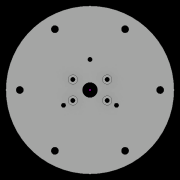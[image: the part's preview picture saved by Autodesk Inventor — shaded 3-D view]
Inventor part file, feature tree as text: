
AUTODESK INVENTOR PART (.ipt)
format: ipt  version: 2022.2 (Build 262287010, 287A)  size: 654,848 bytes
history: native  units: mm
features: extrude x31, sketch x22, other x19, pattern_circular x11, plane x8, fillet x2, move_body x2, revolve x2, draft x2, chamfer x2
ambient origin geometry x8: Origin, YZ Plane, XZ Plane, XY Plane, X Axis, Y Axis, Z Axis, Center Point
bodies: Solid5 (feature_tree)
feature tree (101):
  other  "CrossSection1"
  sketch  "Sketch7"  dims[d167=8.972256mm]
  other  "Roller1"
  other  "Roller2"
  sketch  "Sketch22"  dims[d173=10.814812mm]
  sketch  "Sketch2"  dims[d57=4.025mm d90=61.984365mm]
  sketch  "Sketch23"  dims[d201=75.0mm d232=0.0mm d233=3600.0mm]
  other  "RevRoller1"
  fillet  "Fillet1"  Radius=59.246882mm
  extrude  "Extrusion39"  Depth=61.984365mm
  pattern_circular  "Circular Pattern13"  Count=360  [1 undecoded]
  move_body  "Move Body7"
  revolve  "Revolution13"  [1 undecoded]
  fillet  "Fillet3"  Radius=0.025mm
  pattern_circular  "Circular Pattern14"  Count=24  [1 undecoded]
  move_body  "Move Body6"
  revolve  "Revolution14"  [1 undecoded]
  other  "OuterRim_Top2"
  other  "OuterRim_Bottom2"
  plane  "Work Plane8"
  sketch  "Sketch49"  dims[d352=0.025mm]
  sketch  "Sketch50"  dims[d354=0.025mm]
  sketch  "Sketch51"  dims[d355=16.1595mm]
  extrude  "Extrusion40"  Depth=0.025mm
  extrude  "Extrusion41"  Depth=1.308997mm
  extrude  "Extrusion42"  Depth=0.5mm
  extrude  "Extrusion43"  TaperAngle=360.0deg  [1 undecoded]
  sketch  "Sketch52"  dims[d356=16.159664mm]
  extrude  "Extrusion44"  TaperAngle=90.0deg  [1 undecoded]
  extrude  "Extrusion45"  Depth=2.0mm
  extrude  "Extrusion46"  Depth=2.0mm
  extrude  "Extrusion47"  Depth=2.0mm
  pattern_circular  "Circular Pattern32"  [2 undecoded]
  pattern_circular  "Circular Pattern33"  [2 undecoded]
  sketch  "Sketch57"  dims[d358=360.0deg]
  extrude  "Extrusion50"  Depth=2.0mm
  extrude  "Extrusion51"  TaperAngle=0.0deg  [1 undecoded]
  pattern_circular  "Circular Pattern34"  [2 undecoded]
  extrude  "Extrusion52"  Depth=2.0mm
  extrude  "Extrusion53"  Depth=2.0mm
  pattern_circular  "Circular Pattern35"  [2 undecoded]
  plane  "Work Plane9"
  extrude  "Extrusion54"  Depth=2.0mm
  plane  "Work Plane10"
  sketch  "Sketch60"  dims[d367=8.1mm d370=0.025mm]
  plane  "Work Plane11"
  sketch  "Sketch61"  dims[d371=1.0mm d372=1.308997mm]
  plane  "Work Plane12"
  sketch  "Sketch62"  dims[d373=90.0deg d374=0.5mm]
  extrude  "Extrusion57"  Depth=2.0mm
  extrude  "Extrusion58"  Depth=2.0mm
  plane  "Work Plane7"
  sketch  "Sketch47"  dims[d350=47.575427mm]
  extrude  "Rotor_Ring"  TaperAngle=90.0deg  [1 undecoded]
  draft  "FaceDraft2"
  sketch  "Sketch30"  dims[d343=16.1595mm d344=16.159664mm d345=0.025mm]
  plane  "Work Plane5"
  other  "Rotor Featurs"
  other  "RotorRim_Bottom"
  extrude  "Extrusion24"  TaperAngle=90.0deg  [1 undecoded]
  extrude  "Extrusion25"  TaperAngle=90.0deg  [1 undecoded]
  extrude  "Extrusion26"  Depth=2.0mm
  pattern_circular  "Circular Pattern23"  [2 undecoded]
  sketch  "Sketch41"  dims[d347=0.1mm]
  extrude  "Extrusion27"  TaperAngle=0.0deg  [1 undecoded]
  extrude  "Extrusion28"  Depth=2.0mm
  pattern_circular  "Circular Pattern24"  Count=2  [1 undecoded]
  extrude  "Extrusion29"  Depth=2.5mm
  extrude  "Extrusion30"  Depth=2.0mm
  extrude  "Extrusion31"  Depth=2.0mm
  pattern_circular  "Circular Pattern25"  Angle=30.0deg  [1 undecoded]
  sketch  "Sketch42"  dims[d348=0.1mm]
  extrude  "Extrusion32"  Depth=2.0mm
  extrude  "Extrusion33"  Depth=2.0mm TaperAngle=30.0deg
  extrude  "Extrusion34"  Depth=2.0mm
  extrude  "Extrusion35"  Depth=2.0mm
  pattern_circular  "Circular Pattern26"  [2 undecoded]
  pattern_circular  "Circular Pattern27"  Count=10  [1 undecoded]
  chamfer  "Chamfer1"  Distance=2.0mm
  chamfer  "Chamfer2"  Distance=150.0mm
  draft  "FaceDraft4"
  plane  "Work Plane6"
  sketch  "Sketch43"  dims[d349=47.575591mm]
  extrude  "Extrusion37"  Depth=50.0mm
  extrude  "Extrusion38"  Depth=2.0mm
  other  "2D Equation Curve1"
  sketch  "Sketch40"  dims[d346=0.025mm]
  other  "Work Axis6"
  other  "Work Axis7"
  other  "Work Axis8"
  other  "Work Axis9"
  other  "Work Axis10"
  other  "Work Point1"
  other  "Work Point2"
  other  "Work Point3"
  other  "Work Point4"
  other  "Work Point5"
  sketch  "Sketch48"  dims[d351=0.025mm]
  sketch  "Sketch58"  dims[d359=0.5mm d360=240.0mm]
  sketch  "Sketch59"  dims[d361=360.0deg d363=1.308997mm]
  sketch  "Sketch64"  dims[d375=240.0mm d376=360.0deg d378=90.0deg d379=0.1mm d380=0.025mm d381=0.025mm d382=0.025mm d383=0.025mm d384=11.193516mm d385=0.0mm d386=0.0mm d391=25.0mm d392=75.0mm d393=1.5mm d394=1.5mm d395=1.5mm d396=1.5mm d397=90.0deg d398=90.0deg d399=90.0deg d400=75.0mm d401=11.193516mm d402=0.0mm d486=0.436332mm d487=0.5mm d488=2.0mm d489=0.0mm d490=20.0mm d495=2.5mm d496=8.0mm d506=13.856406mm d507=55.5mm d508=8.0mm d509=0.05mm d510=2.5mm d511=30.0deg d512=12.0mm d513=6.0mm d514=0.2mm d515=30.0deg d516=131.0mm d517=65.5mm d518=0.2mm d519=100.0mm d520=120.0mm d521=2.0mm d522=150.0mm d530=50.0mm d531=5.5mm d532=5.5mm d533=5.5mm d534=85.75mm d535=73.5mm d536=61.25mm d537=24.5mm d538=3.0mm d539=2.4mm d540=0.0mm d541=0.0mm d542=0.0mm d543=5.5mm d544=3.0mm d545=0.0mm d546=90.0mm d547=360.0deg d549=3.0mm d550=3.0mm d551=2.4mm d552=0.0mm d553=5.596758mm d554=0.0mm d555=2.4mm d556=0.0mm d557=5.596758mm d558=0.0mm d559=5.596758mm d560=0.0mm d561=90.0mm d562=360.0deg d564=60.0mm d565=360.0deg d567=5.5mm d568=5.5mm d569=3.0mm d570=0.0mm d571=5.596758mm d572=0.0mm d573=3.0mm d574=0.0mm d575=5.596758mm d576=0.0mm d577=90.0mm d578=360.0deg d580=60.0mm d581=360.0deg d584=20.0mm d585=8.0mm d587=1.75mm d589=3.0mm d592=2.0mm d593=12.0mm d594=12.0mm d600=0.5mm d601=2.0mm d602=45.0deg d603=0.5mm d604=2.0mm d605=45.0deg d606=0.436332mm d607=0.5mm d608=0.0mm d609=20.0mm d611=360.0deg d613=0.0mm d614=0.0mm d617=0.99971mm d618=100.0mm d620=69.0mm d621=5.0mm d622=0.5mm d623=0.5mm d624=5.0mm d625=0.2mm d626=0.0mm d627=20.0mm d629=69.0mm d630=73.5mm d631=20.0mm d633=6.283185mm d635=5.5mm d636=3.0mm d637=7.0mm d638=4.0mm d639=5.596758mm d640=0.0mm d641=3.0mm d642=0.0mm d643=5.596758mm d644=0.0mm d645=4.0mm d646=0.0mm d647=20.0mm d649=6.283185mm d651=3.0mm d652=4.0mm d653=20.0mm d655=6.283185mm d657=7.0mm d658=5.5mm d659=5.596758mm d660=0.0mm d661=2.593516mm d662=0.0mm d663=5.596758mm d664=0.0mm d665=3.193516mm d666=0.0mm d679=50.0mm d680=360.0deg d682=50.0mm d683=360.0deg d694=6.35mm d695=6.35mm d696=6.9mm d697=5.9mm d698=11.194mm d699=0.0mm d700=8.194mm d701=0.0mm d702=60.0mm d703=360.0deg d705=30.0deg d706=4.0mm d707=7.0mm d708=3.193516mm d709=0.0mm d710=11.193516mm d711=0.0mm d712=60.0mm d713=360.0deg d715=20.0mm d717=60.0deg d718=5.0mm d719=0.0mm d720=1.0mm d721=50.0mm d726=5.0mm d727=0.0mm d734=18.0mm d735=11.0mm d736=2.5mm d737=2.5mm d738=2.5mm d739=2.5mm d743=5.0mm d744=5.0mm d745=5.0mm d746=5.0mm d747=2.0mm d748=0.0mm d16=0.872665mm d17=0.872665mm d49=0.872665mm d50=0.872665mm d51=0.872665mm d52=0.872665mm d236=0.5mm d237=0.872665mm d238=0.5mm d239=0.872665mm d282=1.0mm d283=1.0mm d284=1.0mm d285=0.15mm d286=0.25mm d287=0.375mm d288=14.3117mm d289=0.75mm d290=20.594885mm d291=0.0625mm d292=0.75mm d293=0.375mm d405=0.5mm d406=0.872665mm d407=0.5mm d408=0.872665mm d413=0.5mm d414=0.872665mm d415=0.5mm d416=0.872665mm d417=0.5mm d418=0.872665mm d419=0.5mm d420=0.872665mm d421=0.872665mm d431=0.5mm d432=0.872665mm d433=0.5mm d434=0.872665mm d471=0.5mm d472=0.872665mm d473=0.5mm d474=0.872665mm d497=0.5mm d498=0.872665mm d499=0.5mm d500=0.872665mm d590=0.5mm d591=0.872665mm]
note: 26 required parameter values undecoded (feature->parameter linkage not recoverable at this tier; creation-order binding heuristic only, values carry confidence <= 0.55)